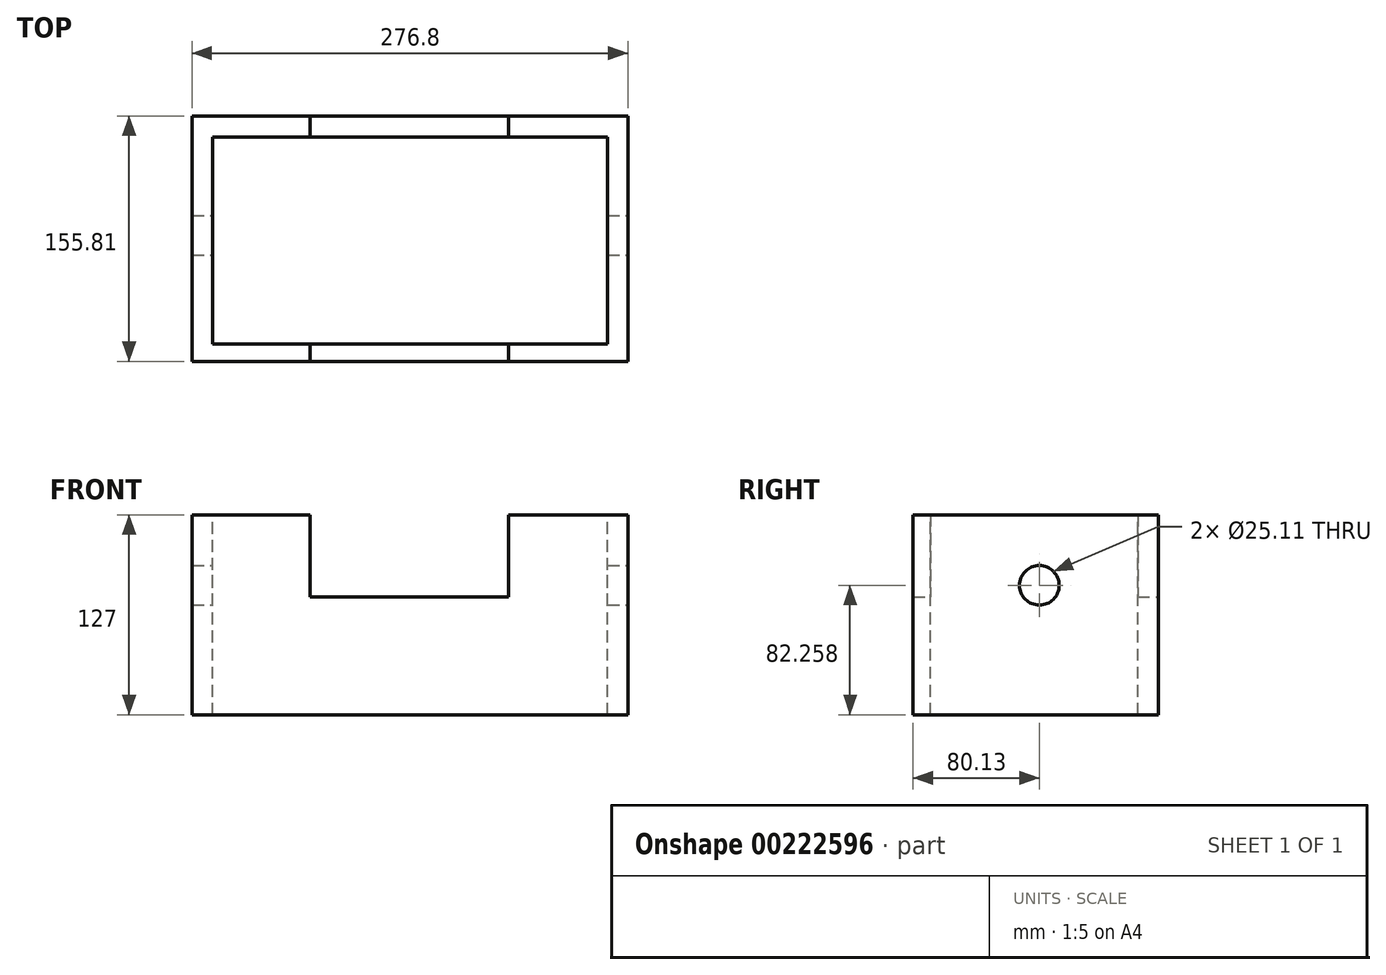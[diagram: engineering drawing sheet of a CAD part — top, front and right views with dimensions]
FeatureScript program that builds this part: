
annotation { "Feature Type Name" : "Feature", "Feature Type Description" : "" }
export const myFeature = defineFeature(function(context is Context, id is Id, definition is map)
    precondition{}
    {
        {
            var Q0;
            Q0=qCreatedBy(makeId("Top.planeOp"),FACE);
            var sketch = newSketch(context, id + "F0", { "sketchPlane" : qUnion([Q0])});
            skLineSegment(sketch, "E0.bottom", {"start": v(-143.37, 75.68) * mm, "end": v(133.43, 75.68) * mm});
            skLineSegment(sketch, "E0.top", {"start": v(-143.37, -80.13) * mm, "end": v(133.43, -80.13) * mm});
            skLineSegment(sketch, "E0.left", {"start": v(-143.37, 75.68) * mm, "end": v(-143.37, -80.13) * mm});
            skLineSegment(sketch, "E0.right", {"start": v(133.43, 75.68) * mm, "end": v(133.43, -80.13) * mm});
            skSolve(sketch);
        }
        {
            var Q0;
            Q0 = qSketchRegion(id + "F0", true);
            extrude(context, id + "F1", {"entities" : qUnion([Q0]), "depth" : 127 * mm});
        }
        {
            var Q0;
            Q0=makeQuery(id+"F1.opExtrude","SWEPT_FACE",FACE,{"disambiguationData":[OSD([sQuery(id+"F0.wireOp",EDGE,"E0.right")])]});
            var sketch = newSketch(context, id + "F2", { "sketchPlane" : qUnion([Q0])});
            skCircle(sketch, "E1", {"center": v(0, 82.26) * mm, "radius": 12.55 * mm});
            skSolve(sketch);
        }
        {
            var Q0;
            Q0 = qSketchRegion(id + "F2", true);
            extrude(context, id + "F3", {"entities" : qUnion([Q0]), "operationType" : NewBodyOperationType.REMOVE, "endBound" : BoundingType.THROUGH_ALL, "oppositeDirection" : true, "depth" : 25.4 * mm});
        }
        {
            var Q0;
            Q0=makeQuery(id+"F1.opExtrude","SWEPT_FACE",FACE,{"disambiguationData":[OSD([sQuery(id+"F0.wireOp",EDGE,"E0.bottom")])]});
            var sketch = newSketch(context, id + "F4", { "sketchPlane" : qUnion([Q0])});
            skLineSegment(sketch, "E2.bottom", {"start": v(-57.78, 127) * mm, "end": v(68.48, 127) * mm});
            skLineSegment(sketch, "E2.top", {"start": v(-57.78, 75.03) * mm, "end": v(68.48, 75.03) * mm});
            skLineSegment(sketch, "E2.left", {"start": v(-57.78, 127) * mm, "end": v(-57.78, 75.03) * mm});
            skLineSegment(sketch, "E2.right", {"start": v(68.48, 127) * mm, "end": v(68.48, 75.03) * mm});
            skSolve(sketch);
        }
        {
            var Q0;
            Q0 = qSketchRegion(id + "F4", true);
            extrude(context, id + "F5", {"entities" : qUnion([Q0]), "operationType" : NewBodyOperationType.REMOVE, "endBound" : BoundingType.THROUGH_ALL, "oppositeDirection" : true, "depth" : 25.4 * mm});
        }
        {
            var Q0;
            Q0=makeQuery(id+"F5.boolean.opBoolean","COPY",FACE,{"disambiguationData":[TD([makeQuery(id+"F1.opExtrude","SWEPT_FACE",FACE,{"disambiguationData":[OSD([sQuery(id+"F0.wireOp",EDGE,"E0.top")])]})])],"derivedFrom":makeQuery(id+"F5.opExtrude","SWEPT_FACE",FACE,{"disambiguationData":[OSD([sQuery(id+"F4.wireOp",EDGE,"E2.top")])]})});
            var sketch = newSketch(context, id + "F6", { "sketchPlane" : qUnion([Q0])});
            skLineSegment(sketch, "E3.bottom", {"start": v(120.53, -69.09) * mm, "end": v(-130.48, -69.09) * mm});
            skLineSegment(sketch, "E3.top", {"start": v(120.53, 62.5) * mm, "end": v(-130.48, 62.5) * mm});
            skLineSegment(sketch, "E3.left", {"start": v(120.53, -69.09) * mm, "end": v(120.53, 62.5) * mm});
            skLineSegment(sketch, "E3.right", {"start": v(-130.48, -69.09) * mm, "end": v(-130.48, 62.5) * mm});
            skSolve(sketch);
        }
        {
            var Q0;
            Q0 = qSketchRegion(id + "F6", true);
            extrude(context, id + "F7", {"entities" : qUnion([Q0]), "operationType" : NewBodyOperationType.REMOVE, "endBound" : BoundingType.THROUGH_ALL, "oppositeDirection" : true, "depth" : 25.4 * mm});
        }
        {
            var Q0;
            {var subQ0=sQuery(id+"F6.wireOp",EDGE,"E3.bottom");var subQ1=makeQuery(id+"F3.boolean.opBoolean","COPY",FACE,{"derivedFrom":makeQuery(id+"F3.opExtrude","SWEPT_FACE",FACE,{"disambiguationData":[OSD([sQuery(id+"F2.wireOp",EDGE,"E1")])]})});var subQ2=makeQuery(id+"F5.opExtrude","SWEPT_FACE",FACE,{"disambiguationData":[OSD([sQuery(id+"F4.wireOp",EDGE,"E2.right")])]});var subQ3=sQuery(id+"F6.wireOp",EDGE,"E3.right");Q0=makeQuery(id+"F7.boolean.opBoolean","COPY",FACE,{"disambiguationData":[TD([subQ1,makeQuery(id+"F5.boolean.opBoolean","COPY",FACE,{"derivedFrom":subQ2}),makeQuery(id+"F5.boolean.opBoolean","COPY",FACE,{"disambiguationData":[TD([makeQuery(id+"F1.opExtrude","SWEPT_FACE",FACE,{"disambiguationData":[OSD([sQuery(id+"F0.wireOp",EDGE,"E0.top")])]})])],"derivedFrom":makeQuery(id+"F5.opExtrude","SWEPT_FACE",FACE,{"disambiguationData":[OSD([sQuery(id+"F4.wireOp",EDGE,"E2.top")])]})}),makeQuery(id+"F7.opExtrude","SWEPT_FACE",FACE,{"disambiguationData":[OSD([subQ0])]}),makeQuery(id+"F7.opExtrude","SWEPT_FACE",FACE,{"disambiguationData":[OSD([subQ3])]})])],"derivedFrom":makeQuery(id+"F7.opExtrude","CAP_FACE",FACE,{"disambiguationData":[OSD([subQ0,sQuery(id+"F6.wireOp",EDGE,"E3.top"),sQuery(id+"F6.wireOp",EDGE,"E3.left"),subQ3])],"isStart":true})});}
            var sketch = newSketch(context, id + "F8", { "sketchPlane" : qUnion([Q0])});
            skLineSegment(sketch, "E4.bottom", {"start": v(-130.48, 69.09) * mm, "end": v(-68.48, 69.09) * mm});
            skLineSegment(sketch, "E4.top", {"start": v(-130.48, 10.27) * mm, "end": v(-68.48, 10.27) * mm});
            skLineSegment(sketch, "E4.left", {"start": v(-130.48, 69.09) * mm, "end": v(-130.48, 10.27) * mm});
            skLineSegment(sketch, "E4.right", {"start": v(-68.48, 69.09) * mm, "end": v(-68.48, 10.27) * mm});
            skSolve(sketch);
        }
        {
            var Q0;
            Q0 = qSketchRegion(id + "F8", true);
            extrude(context, id + "F9", {"entities" : qUnion([Q0]), "operationType" : NewBodyOperationType.REMOVE, "endBound" : BoundingType.THROUGH_ALL, "oppositeDirection" : true, "depth" : 25.4 * mm});
        }
        {
            var Q0;
            {var subQ0=sQuery(id+"F6.wireOp",EDGE,"E3.top");var subQ1=makeQuery(id+"F3.boolean.opBoolean","COPY",FACE,{"derivedFrom":makeQuery(id+"F3.opExtrude","SWEPT_FACE",FACE,{"disambiguationData":[OSD([sQuery(id+"F2.wireOp",EDGE,"E1")])]})});var subQ2=makeQuery(id+"F5.opExtrude","SWEPT_FACE",FACE,{"disambiguationData":[OSD([sQuery(id+"F4.wireOp",EDGE,"E2.right")])]});var subQ3=sQuery(id+"F6.wireOp",EDGE,"E3.right");Q0=makeQuery(id+"F7.boolean.opBoolean","COPY",FACE,{"disambiguationData":[TD([subQ1,makeQuery(id+"F5.boolean.opBoolean","COPY",FACE,{"derivedFrom":subQ2}),makeQuery(id+"F5.boolean.opBoolean","COPY",FACE,{"disambiguationData":[TD([makeQuery(id+"F1.opExtrude","SWEPT_FACE",FACE,{"disambiguationData":[OSD([sQuery(id+"F0.wireOp",EDGE,"E0.bottom")])]})])],"derivedFrom":makeQuery(id+"F5.opExtrude","SWEPT_FACE",FACE,{"disambiguationData":[OSD([sQuery(id+"F4.wireOp",EDGE,"E2.top")])]})}),makeQuery(id+"F7.opExtrude","SWEPT_FACE",FACE,{"disambiguationData":[OSD([subQ0])]}),makeQuery(id+"F7.opExtrude","SWEPT_FACE",FACE,{"disambiguationData":[OSD([subQ3])]})])],"derivedFrom":makeQuery(id+"F7.opExtrude","CAP_FACE",FACE,{"disambiguationData":[OSD([sQuery(id+"F6.wireOp",EDGE,"E3.bottom"),subQ0,sQuery(id+"F6.wireOp",EDGE,"E3.left"),subQ3])],"isStart":true})});}
            var sketch = newSketch(context, id + "F10", { "sketchPlane" : qUnion([Q0])});
            skLineSegment(sketch, "E5.bottom", {"start": v(-130.48, -10.27) * mm, "end": v(-68.48, -10.27) * mm});
            skLineSegment(sketch, "E5.top", {"start": v(-130.48, -62.5) * mm, "end": v(-68.48, -62.5) * mm});
            skLineSegment(sketch, "E5.left", {"start": v(-130.48, -10.27) * mm, "end": v(-130.48, -62.5) * mm});
            skLineSegment(sketch, "E5.right", {"start": v(-68.48, -10.27) * mm, "end": v(-68.48, -62.5) * mm});
            skSolve(sketch);
        }
        {
            var Q0;
            Q0 = qSketchRegion(id + "F10", true);
            extrude(context, id + "F11", {"entities" : qUnion([Q0]), "operationType" : NewBodyOperationType.REMOVE, "endBound" : BoundingType.THROUGH_ALL, "oppositeDirection" : true, "depth" : 25.4 * mm});
        }
        {
            var Q0;
            {var subQ0=makeQuery(id+"F3.boolean.opBoolean","COPY",FACE,{"derivedFrom":makeQuery(id+"F3.opExtrude","SWEPT_FACE",FACE,{"disambiguationData":[OSD([sQuery(id+"F2.wireOp",EDGE,"E1")])]})});var subQ1=makeQuery(id+"F5.opExtrude","SWEPT_FACE",FACE,{"disambiguationData":[OSD([sQuery(id+"F4.wireOp",EDGE,"E2.left")])]});var subQ2=sQuery(id+"F6.wireOp",EDGE,"E3.bottom");var subQ3=sQuery(id+"F6.wireOp",EDGE,"E3.left");Q0=makeQuery(id+"F7.boolean.opBoolean","COPY",FACE,{"disambiguationData":[TD([subQ0,makeQuery(id+"F5.boolean.opBoolean","COPY",FACE,{"derivedFrom":subQ1}),makeQuery(id+"F5.boolean.opBoolean","COPY",FACE,{"disambiguationData":[TD([makeQuery(id+"F1.opExtrude","SWEPT_FACE",FACE,{"disambiguationData":[OSD([sQuery(id+"F0.wireOp",EDGE,"E0.top")])]})])],"derivedFrom":makeQuery(id+"F5.opExtrude","SWEPT_FACE",FACE,{"disambiguationData":[OSD([sQuery(id+"F4.wireOp",EDGE,"E2.top")])]})}),makeQuery(id+"F7.opExtrude","SWEPT_FACE",FACE,{"disambiguationData":[OSD([subQ2])]}),makeQuery(id+"F7.opExtrude","SWEPT_FACE",FACE,{"disambiguationData":[OSD([subQ3])]})])],"derivedFrom":makeQuery(id+"F7.opExtrude","CAP_FACE",FACE,{"disambiguationData":[OSD([subQ2,sQuery(id+"F6.wireOp",EDGE,"E3.top"),subQ3,sQuery(id+"F6.wireOp",EDGE,"E3.right")])],"isStart":true})});}
            var sketch = newSketch(context, id + "F12", { "sketchPlane" : qUnion([Q0])});
            skLineSegment(sketch, "E6.bottom", {"start": v(57.78, 69.09) * mm, "end": v(120.53, 69.09) * mm});
            skLineSegment(sketch, "E6.top", {"start": v(57.78, 10.27) * mm, "end": v(120.53, 10.27) * mm});
            skLineSegment(sketch, "E6.left", {"start": v(57.78, 69.09) * mm, "end": v(57.78, 10.27) * mm});
            skLineSegment(sketch, "E6.right", {"start": v(120.53, 69.09) * mm, "end": v(120.53, 10.27) * mm});
            skSolve(sketch);
        }
        {
            var Q0;
            Q0 = qSketchRegion(id + "F12", true);
            extrude(context, id + "F13", {"entities" : qUnion([Q0]), "operationType" : NewBodyOperationType.REMOVE, "endBound" : BoundingType.THROUGH_ALL, "oppositeDirection" : true, "depth" : 25.4 * mm});
        }
        {
            var Q0;
            {var subQ0=sQuery(id+"F6.wireOp",EDGE,"E3.top");var subQ1=makeQuery(id+"F3.boolean.opBoolean","COPY",FACE,{"derivedFrom":makeQuery(id+"F3.opExtrude","SWEPT_FACE",FACE,{"disambiguationData":[OSD([sQuery(id+"F2.wireOp",EDGE,"E1")])]})});var subQ2=makeQuery(id+"F5.opExtrude","SWEPT_FACE",FACE,{"disambiguationData":[OSD([sQuery(id+"F4.wireOp",EDGE,"E2.left")])]});var subQ3=sQuery(id+"F6.wireOp",EDGE,"E3.left");Q0=makeQuery(id+"F7.boolean.opBoolean","COPY",FACE,{"disambiguationData":[TD([subQ1,makeQuery(id+"F5.boolean.opBoolean","COPY",FACE,{"derivedFrom":subQ2}),makeQuery(id+"F5.boolean.opBoolean","COPY",FACE,{"disambiguationData":[TD([makeQuery(id+"F1.opExtrude","SWEPT_FACE",FACE,{"disambiguationData":[OSD([sQuery(id+"F0.wireOp",EDGE,"E0.bottom")])]})])],"derivedFrom":makeQuery(id+"F5.opExtrude","SWEPT_FACE",FACE,{"disambiguationData":[OSD([sQuery(id+"F4.wireOp",EDGE,"E2.top")])]})}),makeQuery(id+"F7.opExtrude","SWEPT_FACE",FACE,{"disambiguationData":[OSD([subQ0])]}),makeQuery(id+"F7.opExtrude","SWEPT_FACE",FACE,{"disambiguationData":[OSD([subQ3])]})])],"derivedFrom":makeQuery(id+"F7.opExtrude","CAP_FACE",FACE,{"disambiguationData":[OSD([sQuery(id+"F6.wireOp",EDGE,"E3.bottom"),subQ0,subQ3,sQuery(id+"F6.wireOp",EDGE,"E3.right")])],"isStart":true})});}
            var sketch = newSketch(context, id + "F14", { "sketchPlane" : qUnion([Q0])});
            skLineSegment(sketch, "E7.bottom", {"start": v(57.78, -10.27) * mm, "end": v(120.53, -10.27) * mm});
            skLineSegment(sketch, "E7.top", {"start": v(57.78, -62.5) * mm, "end": v(120.53, -62.5) * mm});
            skLineSegment(sketch, "E7.left", {"start": v(57.78, -10.27) * mm, "end": v(57.78, -62.5) * mm});
            skLineSegment(sketch, "E7.right", {"start": v(120.53, -10.27) * mm, "end": v(120.53, -62.5) * mm});
            skSolve(sketch);
        }
        {
            var Q0;
            Q0 = qSketchRegion(id + "F14", true);
            extrude(context, id + "F15", {"entities" : qUnion([Q0]), "operationType" : NewBodyOperationType.REMOVE, "endBound" : BoundingType.THROUGH_ALL, "oppositeDirection" : true, "depth" : 25.4 * mm});
        }
        {
            var Q0;
            {var subQ0=sQuery(id+"F0.wireOp",EDGE,"E0.bottom");var subQ1=sQuery(id+"F0.wireOp",EDGE,"E0.top");var subQ2=sQuery(id+"F0.wireOp",EDGE,"E0.left");Q0=makeQuery(id+"F5.boolean.opBoolean","SPLIT",FACE,{"disambiguationData":[TD([makeQuery(id+"F1.opExtrude","SWEPT_FACE",FACE,{"disambiguationData":[OSD([subQ2])]})])],"derivedFrom":makeQuery(id+"F1.opExtrude","CAP_FACE",FACE,{"disambiguationData":[OSD([subQ0,subQ1,subQ2,sQuery(id+"F0.wireOp",EDGE,"E0.right")])],"isStart":false})});}
            var sketch = newSketch(context, id + "F16", { "sketchPlane" : qUnion([Q0])});
            skLineSegment(sketch, "E8.bottom", {"start": v(-68.48, -10.27) * mm, "end": v(-130.48, -10.27) * mm});
            skLineSegment(sketch, "E8.top", {"start": v(-68.48, 10.27) * mm, "end": v(-130.48, 10.27) * mm});
            skLineSegment(sketch, "E8.left", {"start": v(-68.48, -10.27) * mm, "end": v(-68.48, 10.27) * mm});
            skLineSegment(sketch, "E8.right", {"start": v(-130.48, -10.27) * mm, "end": v(-130.48, 10.27) * mm});
            skSolve(sketch);
        }
        {
            var Q0;
            Q0 = qSketchRegion(id + "F16", true);
            extrude(context, id + "F17", {"entities" : qUnion([Q0]), "operationType" : NewBodyOperationType.REMOVE, "endBound" : BoundingType.THROUGH_ALL, "oppositeDirection" : true, "depth" : 25.4 * mm});
        }
        {
            var Q0;
            {var subQ0=sQuery(id+"F0.wireOp",EDGE,"E0.bottom");var subQ1=sQuery(id+"F0.wireOp",EDGE,"E0.top");var subQ2=sQuery(id+"F0.wireOp",EDGE,"E0.right");Q0=makeQuery(id+"F5.boolean.opBoolean","SPLIT",FACE,{"disambiguationData":[TD([makeQuery(id+"F1.opExtrude","SWEPT_FACE",FACE,{"disambiguationData":[OSD([subQ2])]})])],"derivedFrom":makeQuery(id+"F1.opExtrude","CAP_FACE",FACE,{"disambiguationData":[OSD([subQ0,subQ1,sQuery(id+"F0.wireOp",EDGE,"E0.left"),subQ2])],"isStart":false})});}
            var sketch = newSketch(context, id + "F18", { "sketchPlane" : qUnion([Q0])});
            skLineSegment(sketch, "E9.bottom", {"start": v(57.78, 10.27) * mm, "end": v(120.53, 10.27) * mm});
            skLineSegment(sketch, "E9.top", {"start": v(57.78, -10.27) * mm, "end": v(120.53, -10.27) * mm});
            skLineSegment(sketch, "E9.left", {"start": v(57.78, 10.27) * mm, "end": v(57.78, -10.27) * mm});
            skLineSegment(sketch, "E9.right", {"start": v(120.53, 10.27) * mm, "end": v(120.53, -10.27) * mm});
            skSolve(sketch);
        }
        {
            var Q0;
            Q0 = qSketchRegion(id + "F18", true);
            extrude(context, id + "F19", {"entities" : qUnion([Q0]), "operationType" : NewBodyOperationType.REMOVE, "endBound" : BoundingType.THROUGH_ALL, "oppositeDirection" : true, "depth" : 25.4 * mm});
        }
    });
